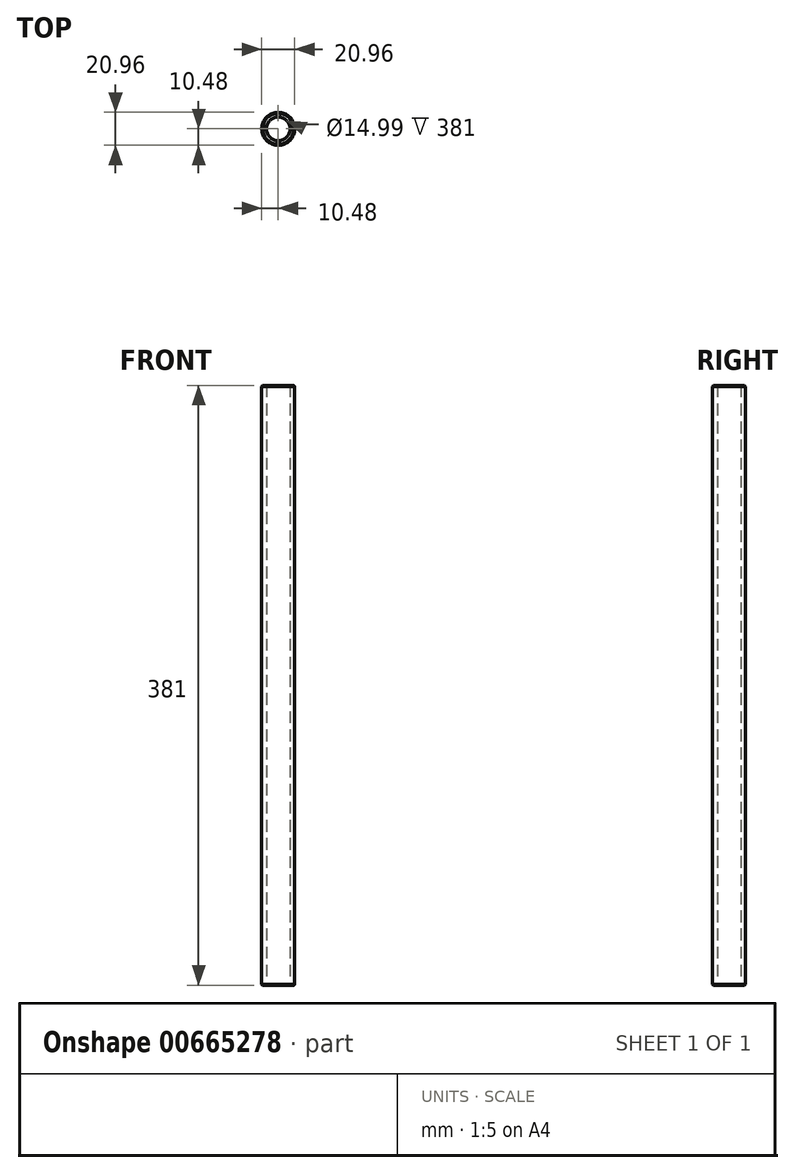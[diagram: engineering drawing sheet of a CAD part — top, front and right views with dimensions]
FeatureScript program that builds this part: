
annotation { "Feature Type Name" : "Feature", "Feature Type Description" : "" }
export const myFeature = defineFeature(function(context is Context, id is Id, definition is map)
    precondition{}
    {
        {
            var Q0;
            Q0=qCreatedBy(makeId("Top.planeOp"),FACE);
            var sketch = newSketch(context, id + "F0", { "sketchPlane" : qUnion([Q0])});
            skCircle(sketch, "E0", {"center": v(0, 0) * mm, "radius": 10.48 * mm});
            skCircle(sketch, "E1", {"center": v(0, 0) * mm, "radius": 7.5 * mm});
            skSolve(sketch);
        }
        {
            var Q0;
            Q0=makeQuery(id+"F0.imprint","IMPRINT",FACE,{"disambiguationData":[TD([[makeQuery(id+"F0.imprint","IMPRINT",EDGE,{"derivedFrom":sQuery(id+"F0.wireOp",EDGE,"E0")}),1.0]])]});
            extrude(context, id + "F1", {"entities" : qUnion([Q0]), "depth" : 381 * mm, "offsetDistance" : 25 * mm});
        }
        {
            var Q0;
            Q0=makeQuery(id+"F1.opExtrude","SWEPT_FACE",FACE,{"disambiguationData":[OSD([sQuery(id+"F0.wireOp",EDGE,"E0")])]});
            chamfer(context, id + "F2", {"entities" : qUnion([Q0]), "width" : 0.64 * mm, "tangentPropagation" : true});
        }
    });
